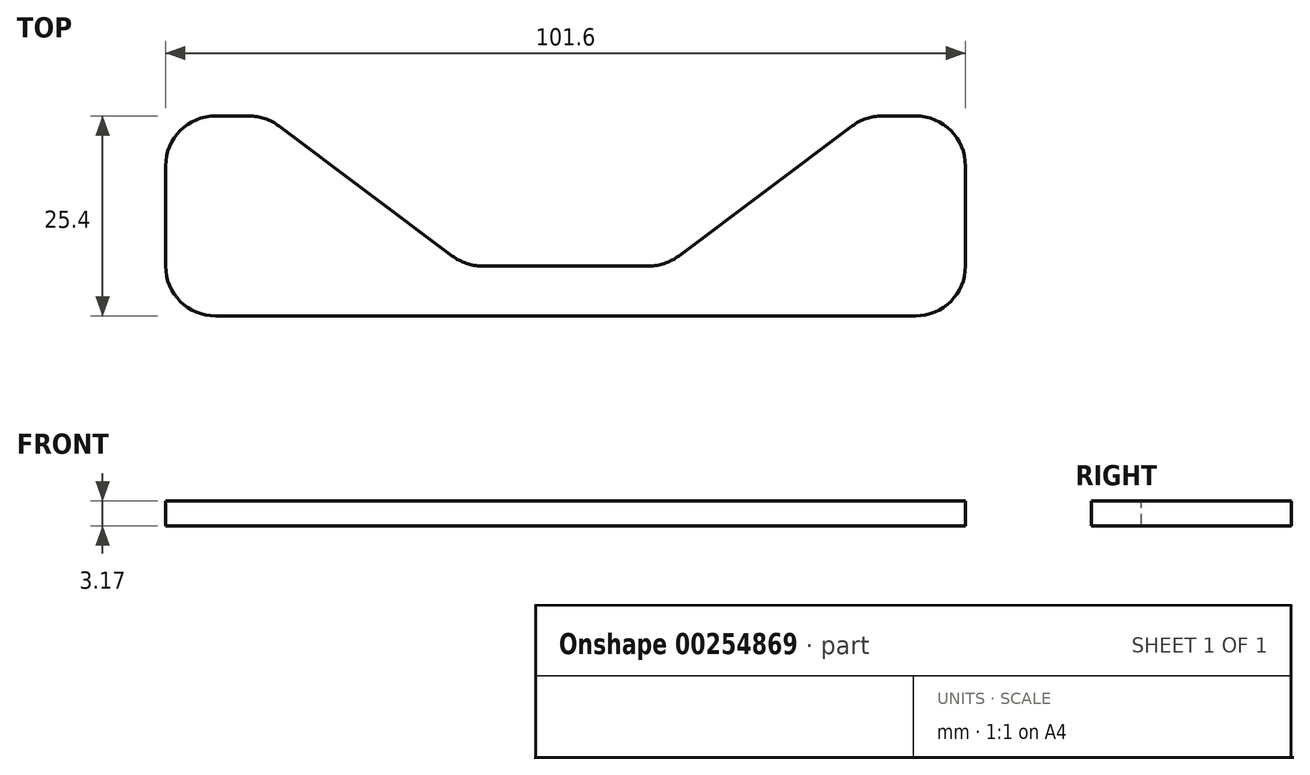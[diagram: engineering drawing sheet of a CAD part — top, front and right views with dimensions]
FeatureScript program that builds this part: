
annotation { "Feature Type Name" : "Feature", "Feature Type Description" : "" }
export const myFeature = defineFeature(function(context is Context, id is Id, definition is map)
    precondition{}
    {
        {
            var Q0;
            Q0=qCreatedBy(makeId("Top.planeOp"),FACE);
            var sketch = newSketch(context, id + "F0", { "sketchPlane" : qUnion([Q0])});
            skLineSegment(sketch, "E0.bottom", {"start": v(-40.22, 12.7) * mm, "end": v(-44.45, 12.7) * mm});
            skLineSegment(sketch, "E0.top", {"start": v(44.45, -12.7) * mm, "end": v(-44.45, -12.7) * mm});
            skLineSegment(sketch, "E0.left", {"start": v(50.8, 6.35) * mm, "end": v(50.8, -6.35) * mm});
            skLineSegment(sketch, "E0.right", {"start": v(-50.8, 6.35) * mm, "end": v(-50.8, -6.35) * mm});
            skPoint(sketch, "E0.middle", {"position": v(0, 0) * mm});
            skPoint(sketch, "E1.visualSharp", {"position": v(-50.8, 12.7) * mm});
            skArc(sketch, "E1.filletArc", {"start": v(-44.45, 12.7) * mm, "mid": v(-48.94, 10.84) * mm, "end": v(-50.8, 6.35) * mm});
            skPoint(sketch, "E2.visualSharp", {"position": v(50.8, 12.7) * mm});
            skArc(sketch, "E2.filletArc", {"start": v(50.8, 6.35) * mm, "mid": v(48.94, 10.84) * mm, "end": v(44.45, 12.7) * mm});
            skPoint(sketch, "E3.visualSharp", {"position": v(50.8, -12.7) * mm});
            skArc(sketch, "E3.filletArc", {"start": v(44.45, -12.7) * mm, "mid": v(48.94, -10.84) * mm, "end": v(50.8, -6.35) * mm});
            skPoint(sketch, "E4.visualSharp", {"position": v(-50.8, -12.7) * mm});
            skArc(sketch, "E4.filletArc", {"start": v(-50.8, -6.35) * mm, "mid": v(-48.94, -10.84) * mm, "end": v(-44.45, -12.7) * mm});
            skLineSegment(sketch, "E5", {"start": v(-10.58, -6.35) * mm, "end": v(10.58, -6.35) * mm});
            skLineSegment(sketch, "E6", {"start": v(44.45, 12.7) * mm, "end": v(40.22, 12.7) * mm});
            skLineSegment(sketch, "E7", {"start": v(-36.4, 11.43) * mm, "end": v(-14.4, -5.08) * mm});
            skLineSegment(sketch, "E8", {"start": v(14.4, -5.08) * mm, "end": v(36.4, 11.43) * mm});
            skArc(sketch, "E9.filletArc", {"start": v(-36.4, 11.43) * mm, "mid": v(-38.2, 12.37) * mm, "end": v(-40.22, 12.7) * mm});
            skArc(sketch, "E10.filletArc", {"start": v(40.22, 12.7) * mm, "mid": v(38.2, 12.37) * mm, "end": v(36.4, 11.43) * mm});
            skPoint(sketch, "E11.visualSharp", {"position": v(-12.7, -6.35) * mm});
            skArc(sketch, "E11.filletArc", {"start": v(-14.4, -5.08) * mm, "mid": v(-12.6, -6.02) * mm, "end": v(-10.58, -6.35) * mm});
            skPoint(sketch, "E12.visualSharp", {"position": v(12.7, -6.35) * mm});
            skArc(sketch, "E12.filletArc", {"start": v(10.58, -6.35) * mm, "mid": v(12.6, -6.02) * mm, "end": v(14.4, -5.08) * mm});
            skSolve(sketch);
        }
        {
            var Q0;
            Q0=makeQuery(id+"F0.imprint","IMPRINT",FACE,{"disambiguationData":[TD([[makeQuery(id+"F0.imprint","IMPRINT",EDGE,{"derivedFrom":sQuery(id+"F0.wireOp",EDGE,"E0.bottom")}),1.0]])]});
            extrude(context, id + "F1", {"entities" : qUnion([Q0]), "oppositeDirection" : true, "depth" : 3.17 * mm});
        }
    });
